# Revit family: LAMP_KOMBIC
name_source: partatom
category: Luminarias
revit_build: Autodesk Revit 2015 (Build: 20140606_1530(x64)
units: mm (PartAtom-declared; Revit-internal decimal feet)

## types (14) — shared parameters
Altura central = 62 mm  [stored 0.203412 ft]
CRI = 80
Cambio de temperatura de color de luz atenuada = <Ninguno>
Comentarios de tipo = Availability of switching between accessories through visibility parameters when placed in a project.
Diam. exterior cuerpo = 167 mm  [stored 0.5479 ft]
Diam. inferior cuerpo = 220 mm  [stored 0.721785 ft]
Diam. inferior interior = 188 mm  [stored 0.616798 ft]
Diameter = 220 mm  [stored 0.721785 ft]
Fabricante = LAMP
Filtro de color = 16777215
Finish = Shiny white
Gear = Electronic
IEE = A+
Installation instructions = http://www.lamp.es
Insulation class = II
Last update = 10/05/2018
Luminaire type = Indoor - Recessed Downlight
MacAdam = 3
Manufacturer URL = http://www.lamp.es
Manufacturer country = Spain
Manufacturer name = LAMP
Material Armazón BL = LAMP_PC Armazón Kombic BL
Material Armazón GR = LAMP_PC Armazón Kombic GR
Material Difusor = LAMP_PMMA Difusor Kombic
Material Disipador = LAMP_Aluminio Disipador Kombic
Model explanation = Availability of switching between accessories through visibility parameters when placed in a project.
Photobiological risk = Group 0
Power Supply = 220-240V 50-60Hz
Product URL = http://www.lamp.es
Product datasheet = http://www.lamp.es
Protection rating = IP44
Recessed diameter = 209 mm  [stored 0.685696 ft]
Ángulo de inclinación = 90.00°

## per-type parameters (varying)
| type | Altura exterior | Archivo de red fotométrica | Descripción | Efficacy | Height | LED Lifetime | Lámpara | Material Reflector | Modelo | Plum | Power | Product code | Type | Weight |
| BRIGHT 2000LM 3000K | 106 mm  [stored 0.347769 ft] | 9241480.ies | KOMBIC BRIGHT 2000 WW | 87 lm/W | 106 mm  [stored 0.347769 ft] | 50.000 L90 B10 | COB LED | LAMP_PC Reflector Kombic Metalizado Brillante | 9241480 | 21 W | 18 W | 9241480 | COB CITIZEN | 0.74 kg |
| BRIGHT 2000LM 4000K | 106 mm  [stored 0.347769 ft] | 9241490.IES | KOMBIC BRIGHT 2000 NW | 90 lm/W | 106 mm  [stored 0.347769 ft] | 50.000 L90 B10 | COB LED | LAMP_PC Reflector Kombic Metalizado Brillante | 9241490 | 21 W | 18 W | 9241490 | COB CITIZEN | 0.74 kg |
| BRIGHT 3000LM 3000K | 106 mm  [stored 0.347769 ft] | 9241350.IES | KOMBIC BRIGHT 3000 WW | 114 lm/W | 106 mm  [stored 0.347769 ft] | 50.000 L80 B10 | MID-POWER LED | LAMP_PC Reflector Kombic Metalizado Brillante | 9241350 | 18 W | 17 W | 9241350 | MID POWER TRIDONIC | 0.98 kg |
| BRIGHT 3000LM 4000K | 106 mm  [stored 0.347769 ft] | 9241360.IES | KOMBIC BRIGHT 3000 NW | 120 lm/W | 106 mm  [stored 0.347769 ft] | 50.000 L80 B10 | MID-POWER LED | LAMP_PC Reflector Kombic Metalizado Brillante | 9241360 | 18 W | 17 W | 9241360 | MID POWER TRIDONIC | 0.98 kg |
| BRIGHT 4000LM 3000K | 106 mm  [stored 0.347769 ft] | 9241370.IES | KOMBIC BRIGHT 4000 WW | 110 lm/W | 106 mm  [stored 0.347769 ft] | 50.000 L80 B10 | MID-POWER LED | LAMP_PC Reflector Kombic Metalizado Brillante | 9241370 | 25 W | 24 W | 9241370 | MID POWER TRIDONIC | 0.98 kg |
| BRIGHT 4000LM 4000K | 106 mm  [stored 0.347769 ft] | 9241380.IES | KOMBIC BRIGHT 4000 NW | 116 lm/W | 106 mm  [stored 0.347769 ft] | 50.000 L80 B10 | MID-POWER LED | LAMP_PC Reflector Kombic Metalizado Brillante | 9241380 | 25 W | 24 W | 9241380 | MID POWER TRIDONIC | 0.98 kg |
| BRIGHT 5000LM 3000K | 120 mm  [stored 0.393701 ft] | 9241520.IES | KOMBIC BRIGHT 5000 WW | 96 lm/W | 120 mm  [stored 0.393701 ft] | 50.000 L70 B10 | COB LED | LAMP_PC Reflector Kombic Metalizado Brillante | 9241520 | 39 W | 36 W | 9241520 | COB PHILIPS | 1.54 kg |
| BRIGHT 5000LM 4000K | 120 mm  [stored 0.393701 ft] | 9241530.IES | KOMBIC BRIGHT 5000 NW | 103 lm/W | 120 mm  [stored 0.393701 ft] | 50.000 L70 B10 | COB LED | LAMP_PC Reflector Kombic Metalizado Brillante | 9241530 | 39 W | 36 W | 9241530 | COB PHILIPS | 1.54 kg |
| MATT 3000LM 3000K | 106 mm  [stored 0.347769 ft] | 9241351.IES | KOMBIC MATT 3000 WW | 110 lm/W | 106 mm  [stored 0.347769 ft] | 50.000 L80 B10 | COB LED | LAMP_PC Reflector Kombic Metalizado Mate | 9241351 | 18 W | 17 W | 9241351 | COB TRIDONIC | 0.98 kg |
| MATT 3000LM 4000K | 106 mm  [stored 0.347769 ft] | 9241361.IES | KOMBIC MATT 3000 NW | 115 lm/W | 106 mm  [stored 0.347769 ft] | 50.000 L80 B10 | COB LED | LAMP_PC Reflector Kombic Metalizado Mate | 9241361 | 18 W | 17 W | 9241361 | COB TRIDONIC | 0.98 kg |
| MATT 4000LM 3000K | 106 mm  [stored 0.347769 ft] | 9241371.IES | KOMBIC MATT 4000 WW | 106 lm/W | 106 mm  [stored 0.347769 ft] | 50.000 L80 B10 | COB LED | LAMP_PC Reflector Kombic Metalizado Mate | 9241371 | 25 W | 24 W | 9241371 | COB TRIDONIC | 0.98 kg |
| MATT 4000LM 4000K | 106 mm  [stored 0.347769 ft] | 9241381.IES | KOMBIC MATT 4000 NW | 111 lm/W | 106 mm  [stored 0.347769 ft] | 50.000 L80 B10 | COB LED | LAMP_PC Reflector Kombic Metalizado Mate | 9241381 | 25 W | 24 W | 9241381 | COB TRIDONIC | 0.98 kg |
| MATT 5000LM 3000K | 120 mm  [stored 0.393701 ft] | 9241521.IES | KOMBIC MATT 5000 WW | 92 lm/W | 120 mm  [stored 0.393701 ft] | 50.000 L70 B10 | COB LED | LAMP_PC Reflector Kombic Metalizado Mate | 9241521 | 39 W | 36 W | 9241521 | COB PHILIPS | 1.54 kg |
| MATT 5000LM 4000K | 120 mm  [stored 0.393701 ft] | 9241531.IES | KOMBIC MATT 5000 NW | 99 lm/W | 120 mm  [stored 0.393701 ft] | 50.000 L70 B10 | COB LED | LAMP_PC Reflector Kombic Metalizado Mate | 9241531 | 39 W | 36 W | 9241531 | COB PHILIPS | 1.54 kg |

note: [stored X ft] marks values corroborated as IEEE doubles in the binary element streams (Revit-internal decimal feet)

## geometry (parser evidence)
native form markers: Blend x2
no freeform markers — native parametric forms only
